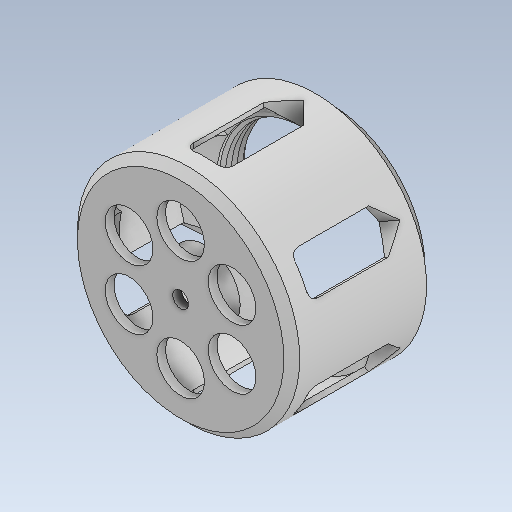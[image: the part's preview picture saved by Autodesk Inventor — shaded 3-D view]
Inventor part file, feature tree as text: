
AUTODESK INVENTOR PART (.ipt)
format: ipt  version: 2020 (Build 240168000, 168)  size: 505,856 bytes
history: native  units: mm
features: sketch x9, extrude x8, chamfer x5, pattern_circular x2, helix x1, fillet x1, thicken_offset x1
ambient origin geometry x8: Origin, YZ Plane, XZ Plane, XY Plane, X Axis, Y Axis, Z Axis, Center Point
bodies: Solid1 (feature_tree)
feature tree (27):
  extrude  "Extrusion1"  Depth=7.0mm
  helix  "Coil1"  [1 undecoded]
  chamfer  "Chamfer1"  Distance=0.475mm Angle=45.0deg
  extrude  "Extrusion2"  Depth=36.0mm
  chamfer  "Chamfer2"  Distance=3.0mm
  extrude  "Extrusion3"  Depth=1.2mm
  extrude  "Extrusion4"  Depth=5.0mm
  chamfer  "Chamfer3"  Distance=12.0mm
  extrude  "Extrusion5"  Depth=5.0mm TaperAngle=360.0deg
  chamfer  "Chamfer4"  Distance=1.2mm
  extrude  "Extrusion6"  Depth=5.0mm TaperAngle=45.0deg
  chamfer  "Chamfer5"  Distance=16.0mm
  fillet  "Fillet1"  Radius=0.8mm
  pattern_circular  "Circular Pattern1"  [2 undecoded]
  extrude  "Extrusion7"  Depth=5.0mm TaperAngle=45.0deg
  thicken_offset  "Thicken1"
  extrude  "Extrusion8"  Depth=10.0mm
  pattern_circular  "Circular Pattern2"  [2 undecoded]
  sketch  "Sketch1"  dims[d0=43.9mm d1=1.6mm d2=7.0mm d3=0.0mm]
  sketch  "Sketch2"  dims[d4=1.2mm]
  sketch  "Sketch3"  dims[d5=0.8mm]
  sketch  "Sketch4"  dims[d6=1.5mm]
  sketch  "Sketch5"  dims[d7=5.8mm d8=10.0mm d9=0.0mm d10=90.0deg d11=90.0deg d12=0.0mm d13=0.0mm d14=0.475mm d15=2.0mm d16=45.0deg]
  sketch  "Sketch6"  dims[d17=56.0mm d18=36.0mm]
  sketch  "Sketch7"  dims[d19=1.2mm d20=3.0mm d21=0.0mm]
  sketch  "Sketch8"  dims[d22=1.45mm d23=2.0mm d24=45.0deg d25=1.2mm]
  sketch  "Sketch9"  dims[d26=30.0mm d27=0.0mm d28=15.0mm d29=12.0mm d30=60.0mm d32=360.0deg d34=1.2mm d35=0.0mm d36=4.85mm d37=2.0mm d38=45.0deg d39=16.0mm d40=0.8mm d41=4.0mm d42=0.0mm d43=1.0mm d44=2.0mm d45=45.0deg d46=10.0mm d47=10.0mm d48=0.0mm d49=5.0mm d50=2.0mm d51=45.0deg d52=2.0mm d53=60.0mm d54=360.0deg d56=4.0mm d57=10.0mm d58=0.0mm d59=1.0mm d60=1.0mm d61=3.0mm d62=2.96706mm d63=0.523599mm d64=1.2mm d65=5.0mm d66=0.0mm d67=30.0mm d68=360.0deg]
note: 5 required parameter values undecoded (feature->parameter linkage not recoverable at this tier; creation-order binding heuristic only, values carry confidence <= 0.55)
